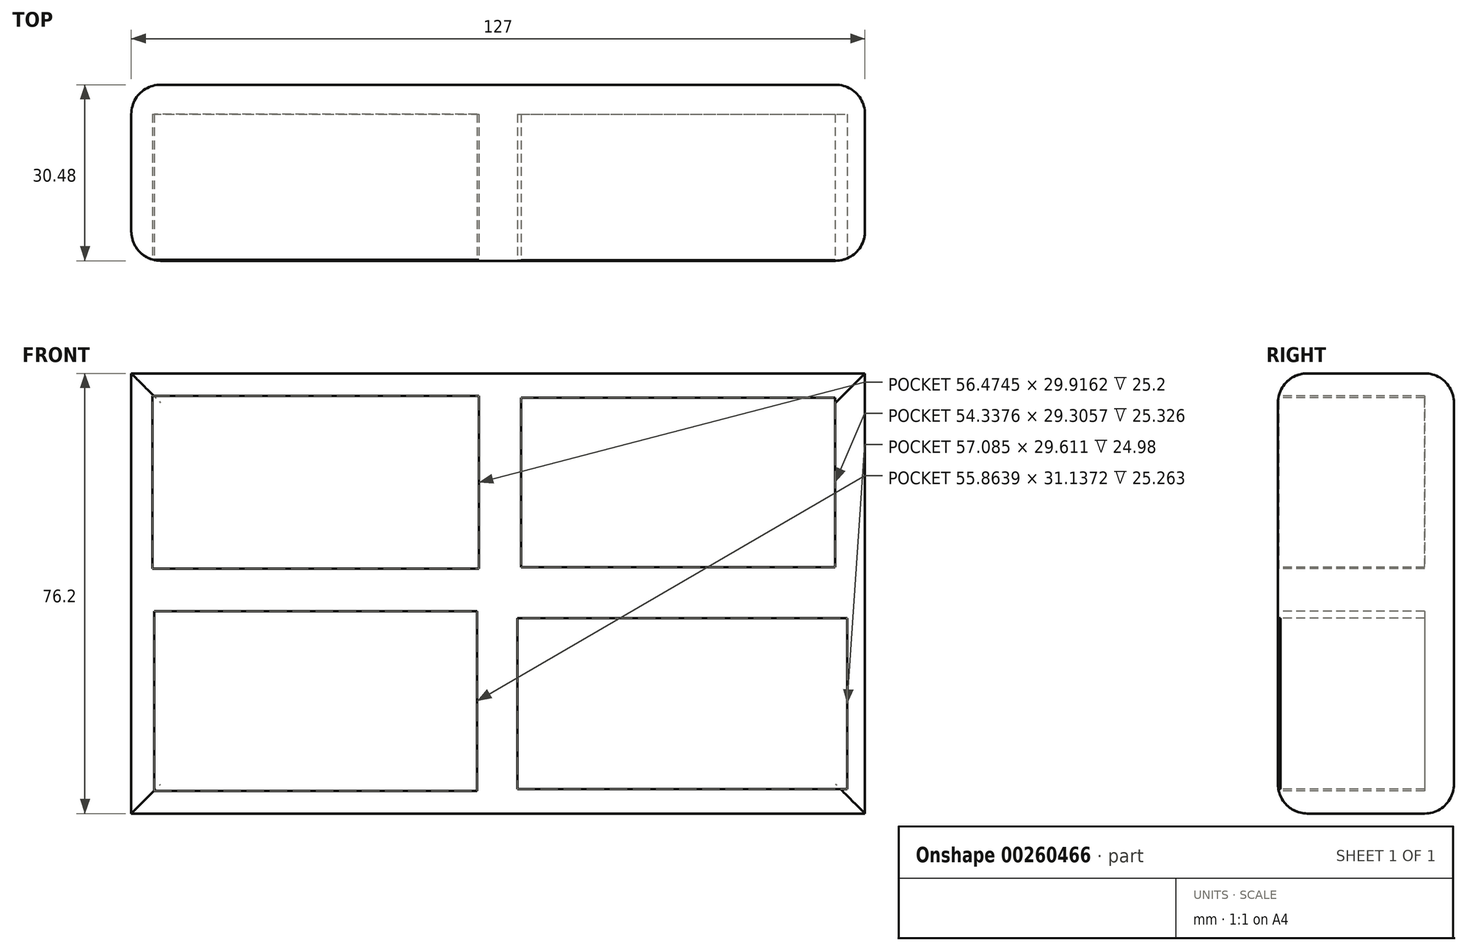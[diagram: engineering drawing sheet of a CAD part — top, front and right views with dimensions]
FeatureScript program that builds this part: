
annotation { "Feature Type Name" : "Feature", "Feature Type Description" : "" }
export const myFeature = defineFeature(function(context is Context, id is Id, definition is map)
    precondition{}
    {
        {
            var Q0;
            Q0=qCreatedBy(makeId("Front.planeOp"),FACE);
            var sketch = newSketch(context, id + "F0", { "sketchPlane" : qUnion([Q0])});
            skLineSegment(sketch, "E0.bottom", {"start": v(63.5, 38.1) * mm, "end": v(-63.5, 38.1) * mm});
            skLineSegment(sketch, "E0.top", {"start": v(63.5, -38.1) * mm, "end": v(-63.5, -38.1) * mm});
            skLineSegment(sketch, "E0.left", {"start": v(63.5, 38.1) * mm, "end": v(63.5, -38.1) * mm});
            skLineSegment(sketch, "E0.right", {"start": v(-63.5, 38.1) * mm, "end": v(-63.5, -38.1) * mm});
            skPoint(sketch, "E0.middle", {"position": v(0, 0) * mm});
            skSolve(sketch);
        }
        {
            var Q0;
            Q0=makeQuery(id+"F0.imprint","IMPRINT",FACE,{"disambiguationData":[TD([[makeQuery(id+"F0.imprint","IMPRINT",EDGE,{"derivedFrom":sQuery(id+"F0.wireOp",EDGE,"E0.bottom")}),1.0]])]});
            extrude(context, id + "F1", {"entities" : qUnion([Q0]), "depth" : 30.48 * mm});
        }
        {
            var Q0;
            Q0=makeQuery(id+"F1.opExtrude","CAP_FACE",FACE,{"disambiguationData":[OSD([sQuery(id+"F0.wireOp",EDGE,"E0.bottom"),sQuery(id+"F0.wireOp",EDGE,"E0.top"),sQuery(id+"F0.wireOp",EDGE,"E0.left"),sQuery(id+"F0.wireOp",EDGE,"E0.right")])],"isStart":false});
            var sketch = newSketch(context, id + "F2", { "sketchPlane" : qUnion([Q0])});
            skLineSegment(sketch, "E1.bottom", {"start": v(-59.83, 34.19) * mm, "end": v(-3.36, 34.19) * mm});
            skLineSegment(sketch, "E1.top", {"start": v(-59.83, 4.27) * mm, "end": v(-3.36, 4.27) * mm});
            skLineSegment(sketch, "E1.left", {"start": v(-59.83, 34.19) * mm, "end": v(-59.83, 4.27) * mm});
            skLineSegment(sketch, "E1.right", {"start": v(-3.36, 34.19) * mm, "end": v(-3.36, 4.27) * mm});
            skLineSegment(sketch, "E2.bottom", {"start": v(-3.66, -3.05) * mm, "end": v(-59.53, -3.05) * mm});
            skLineSegment(sketch, "E2.top", {"start": v(-3.66, -34.19) * mm, "end": v(-59.53, -34.19) * mm});
            skLineSegment(sketch, "E2.left", {"start": v(-3.66, -3.05) * mm, "end": v(-3.66, -34.19) * mm});
            skLineSegment(sketch, "E2.right", {"start": v(-59.53, -3.05) * mm, "end": v(-59.53, -34.19) * mm});
            skLineSegment(sketch, "E3.bottom", {"start": v(3.97, 4.58) * mm, "end": v(58.3, 4.58) * mm});
            skLineSegment(sketch, "E3.top", {"start": v(3.97, 33.88) * mm, "end": v(58.3, 33.88) * mm});
            skLineSegment(sketch, "E3.left", {"start": v(3.97, 4.58) * mm, "end": v(3.97, 33.88) * mm});
            skLineSegment(sketch, "E3.right", {"start": v(58.3, 4.58) * mm, "end": v(58.3, 33.88) * mm});
            skLineSegment(sketch, "E4.bottom", {"start": v(3.36, -4.27) * mm, "end": v(60.44, -4.27) * mm});
            skLineSegment(sketch, "E4.top", {"start": v(3.36, -33.88) * mm, "end": v(60.44, -33.88) * mm});
            skLineSegment(sketch, "E4.left", {"start": v(3.36, -4.27) * mm, "end": v(3.36, -33.88) * mm});
            skLineSegment(sketch, "E4.right", {"start": v(60.44, -4.27) * mm, "end": v(60.44, -33.88) * mm});
            skSolve(sketch);
        }
        {
            var Q0;
            Q0=makeQuery(id+"F2.imprint","IMPRINT",FACE,{"disambiguationData":[TD([[makeQuery(id+"F2.imprint","IMPRINT",EDGE,{"derivedFrom":sQuery(id+"F2.wireOp",EDGE,"E1.bottom")}),-1.0]])]});
            var Q1;
            Q1=makeQuery(id+"F2.imprint","IMPRINT",FACE,{"disambiguationData":[TD([[makeQuery(id+"F2.imprint","IMPRINT",EDGE,{"derivedFrom":sQuery(id+"F2.wireOp",EDGE,"E3.bottom")}),1.0]])]});
            var Q2;
            Q2=makeQuery(id+"F2.imprint","IMPRINT",FACE,{"disambiguationData":[TD([[makeQuery(id+"F2.imprint","IMPRINT",EDGE,{"derivedFrom":sQuery(id+"F2.wireOp",EDGE,"E4.bottom")}),-1.0]])]});
            var Q3;
            Q3=makeQuery(id+"F2.imprint","IMPRINT",FACE,{"disambiguationData":[TD([[makeQuery(id+"F2.imprint","IMPRINT",EDGE,{"derivedFrom":sQuery(id+"F2.wireOp",EDGE,"E2.bottom")}),1.0]])]});
            extrude(context, id + "F3", {"entities" : qUnion([Q0, Q1, Q2, Q3]), "operationType" : NewBodyOperationType.REMOVE, "oppositeDirection" : true, "depth" : 25.4 * mm});
        }
        {
            var Q0;
            Q0=makeQuery(id+"F1.opExtrude","CAP_EDGE",EDGE,{"disambiguationData":[OSD([sQuery(id+"F0.wireOp",EDGE,"E0.top")])],"isStart":false});
            var Q1;
            Q1=makeQuery(id+"F1.opExtrude","CAP_EDGE",EDGE,{"disambiguationData":[OSD([sQuery(id+"F0.wireOp",EDGE,"E0.right")])],"isStart":false});
            var Q2;
            Q2=makeQuery(id+"F1.opExtrude","CAP_EDGE",EDGE,{"disambiguationData":[OSD([sQuery(id+"F0.wireOp",EDGE,"E0.bottom")])],"isStart":false});
            var Q3;
            Q3=makeQuery(id+"F1.opExtrude","CAP_EDGE",EDGE,{"disambiguationData":[OSD([sQuery(id+"F0.wireOp",EDGE,"E0.left")])],"isStart":false});
            var Q4;
            Q4=makeQuery(id+"F1.opExtrude","CAP_EDGE",EDGE,{"disambiguationData":[OSD([sQuery(id+"F0.wireOp",EDGE,"E0.top")])],"isStart":true});
            var Q5;
            Q5=makeQuery(id+"F1.opExtrude","CAP_EDGE",EDGE,{"disambiguationData":[OSD([sQuery(id+"F0.wireOp",EDGE,"E0.right")])],"isStart":true});
            var Q6;
            Q6=makeQuery(id+"F1.opExtrude","CAP_EDGE",EDGE,{"disambiguationData":[OSD([sQuery(id+"F0.wireOp",EDGE,"E0.left")])],"isStart":true});
            var Q7;
            Q7=makeQuery(id+"F1.opExtrude","CAP_EDGE",EDGE,{"disambiguationData":[OSD([sQuery(id+"F0.wireOp",EDGE,"E0.bottom")])],"isStart":true});
            fillet(context, id + "F4", {"entities" : qUnion([Q0, Q1, Q2, Q3, Q4, Q5, Q6, Q7]), "radius" : 5.08 * mm, "tangentPropagation" : true, "allowEdgeOverflow" : false});
        }
    });
